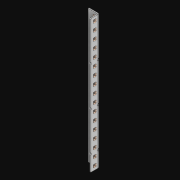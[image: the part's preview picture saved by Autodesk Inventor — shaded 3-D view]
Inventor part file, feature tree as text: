
AUTODESK INVENTOR PART (.ipt)
format: ipt  version: 2021 (Build 250183000, 183)  size: 1,189,376 bytes
history: native  units: in
note: dims shown in document units (in); Inventor stores cm internally (conversion verified against a paired STEP export)
features: extrude x36, other x34, sketch x4, pattern_linear x2, sheet_metal_op x1
ambient origin geometry x8: Origin, YZ Plane, XZ Plane, XY Plane, X Axis, Y Axis, Z Axis, Center Point
bodies: Solid1 (feature_tree)
feature tree (77):
  pattern_linear  "Rectangular Pattern1"  Spacing1=0.5in  [1 undecoded]
  pattern_linear  "Rectangular Pattern3"  Count1=17  [1 undecoded]
  extrude  "Extrusion1"  Depth=0.5in
  extrude  "Extrusion2"  Depth=0.5in
  sketch  "Sketch1"  dims[d0=0.182in]
  other  "Srf1"
  sketch  "Sketch3"  dims[d1=0.063in d2=0.0in]
  other  "Srf3"
  other  "Srf4"
  other  "Srf5"
  other  "Srf6"
  other  "Srf7"
  other  "Srf8"
  other  "Srf9"
  other  "Srf10"
  other  "Srf11"
  other  "Srf12"
  other  "Srf13"
  other  "Srf14"
  other  "Srf15"
  other  "Srf16"
  other  "Srf17"
  other  "Srf18"
  other  "Srf19"
  other  "Srf142"
  other  "Srf143"
  other  "Srf144"
  other  "Srf145"
  other  "Srf146"
  other  "Srf147"
  other  "Srf148"
  other  "Srf149"
  other  "Srf150"
  other  "Srf151"
  other  "Srf152"
  other  "Srf153"
  other  "Srf154"
  other  "Srf155"
  other  "Srf156"
  other  "Srf157"
  sketch  "Sketch4"  dims[d6=0.182in]
  sketch  "Sketch5"  dims[d7=0.063in d8=0.0in d11=0.5in d12=0.3937in d14=0.5in d18=6.6929in d20=0.5in d21=9.0in d22=0.0in d23=0.841in d24=0.0in]
  sheet_metal_op  "Fold1"
  extrude  "ExtrusionSrf1"  TaperAngle=0.0deg  [1 undecoded]
  extrude  "ExtrusionSrf3"  Depth=0.5in TaperAngle=0.0deg
  extrude  "ExtrusionSrf4"  [1 undecoded]
  extrude  "ExtrusionSrf5"  [1 undecoded]
  extrude  "ExtrusionSrf6"  [1 undecoded]
  extrude  "ExtrusionSrf7"  [1 undecoded]
  extrude  "ExtrusionSrf8"  [1 undecoded]
  extrude  "ExtrusionSrf9"  [1 undecoded]
  extrude  "ExtrusionSrf10"  [1 undecoded]
  extrude  "ExtrusionSrf11"  [1 undecoded]
  extrude  "ExtrusionSrf12"  [1 undecoded]
  extrude  "ExtrusionSrf13"  [1 undecoded]
  extrude  "ExtrusionSrf14"  [1 undecoded]
  extrude  "ExtrusionSrf15"  [1 undecoded]
  extrude  "ExtrusionSrf16"  [1 undecoded]
  extrude  "ExtrusionSrf17"  [1 undecoded]
  extrude  "ExtrusionSrf18"  [1 undecoded]
  extrude  "ExtrusionSrf19"  [1 undecoded]
  extrude  "ExtrusionSrf142"  [1 undecoded]
  extrude  "ExtrusionSrf143"  [1 undecoded]
  extrude  "ExtrusionSrf144"  [1 undecoded]
  extrude  "ExtrusionSrf145"  [1 undecoded]
  extrude  "ExtrusionSrf146"  [1 undecoded]
  extrude  "ExtrusionSrf147"  [1 undecoded]
  extrude  "ExtrusionSrf148"  [1 undecoded]
  extrude  "ExtrusionSrf149"  [1 undecoded]
  extrude  "ExtrusionSrf150"  [1 undecoded]
  extrude  "ExtrusionSrf151"  [1 undecoded]
  extrude  "ExtrusionSrf152"  [1 undecoded]
  extrude  "ExtrusionSrf153"  [1 undecoded]
  extrude  "ExtrusionSrf154"  [1 undecoded]
  extrude  "ExtrusionSrf155"  [1 undecoded]
  extrude  "ExtrusionSrf156"  [1 undecoded]
  extrude  "ExtrusionSrf157"  [1 undecoded]
note: 35 required parameter values undecoded (feature->parameter linkage not recoverable at this tier; creation-order binding heuristic only, values carry confidence <= 0.55)
